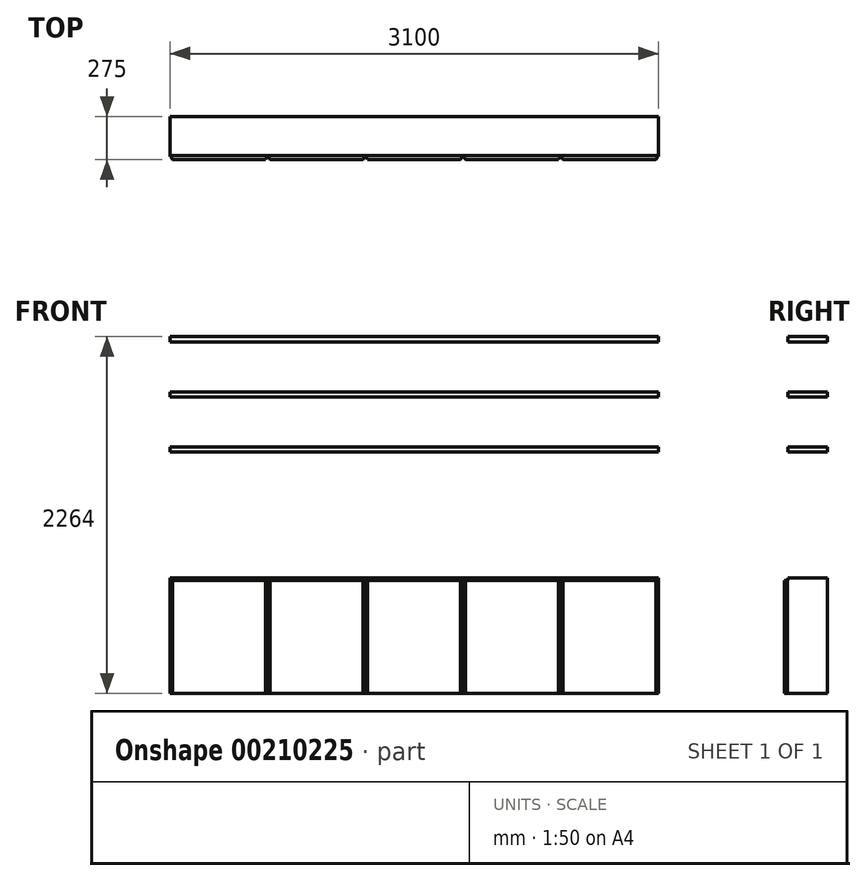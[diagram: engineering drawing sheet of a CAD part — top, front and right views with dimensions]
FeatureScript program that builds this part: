
annotation { "Feature Type Name" : "Feature", "Feature Type Description" : "" }
export const myFeature = defineFeature(function(context is Context, id is Id, definition is map)
    precondition{}
    {
        {
            var Q0;
            Q0=qCreatedBy(makeId("Right.planeOp"),FACE);
            var sketch = newSketch(context, id + "F0", { "sketchPlane" : qUnion([Q0])});
            skLineSegment(sketch, "E0.bottom", {"start": v(-250, 732) * mm, "end": v(0, 732) * mm});
            skLineSegment(sketch, "E0.top", {"start": v(-250, 700) * mm, "end": v(0, 700) * mm});
            skLineSegment(sketch, "E0.left", {"start": v(-250, 732) * mm, "end": v(-250, 700) * mm});
            skLineSegment(sketch, "E0.right", {"start": v(0, 732) * mm, "end": v(0, 700) * mm});
            skLineSegment(sketch, "E1.bottom", {"start": v(-250, 1532) * mm, "end": v(0, 1532) * mm});
            skLineSegment(sketch, "E1.top", {"start": v(-250, 1564) * mm, "end": v(0, 1564) * mm});
            skLineSegment(sketch, "E1.left", {"start": v(-250, 1532) * mm, "end": v(-250, 1564) * mm});
            skLineSegment(sketch, "E1.right", {"start": v(0, 1532) * mm, "end": v(0, 1564) * mm});
            skLineSegment(sketch, "E2.0.1.0", {"start": v(0, 1882) * mm, "end": v(0, 1914) * mm});
            skLineSegment(sketch, "E2.0.1.1", {"start": v(-250, 1882) * mm, "end": v(0, 1882) * mm});
            skLineSegment(sketch, "E2.0.1.2", {"start": v(-250, 1914) * mm, "end": v(0, 1914) * mm});
            skLineSegment(sketch, "E2.0.1.3", {"start": v(-250, 1882) * mm, "end": v(-250, 1914) * mm});
            skLineSegment(sketch, "E2.0.2.0", {"start": v(0, 2232) * mm, "end": v(0, 2264) * mm});
            skLineSegment(sketch, "E2.0.2.1", {"start": v(-250, 2232) * mm, "end": v(0, 2232) * mm});
            skLineSegment(sketch, "E2.0.2.2", {"start": v(-250, 2264) * mm, "end": v(0, 2264) * mm});
            skLineSegment(sketch, "E2.0.2.3", {"start": v(-250, 2232) * mm, "end": v(-250, 2264) * mm});
            skLineSegment(sketch, "E2.direction1", {"start": v(0, 1532) * mm, "end": v(310, 1532) * mm, "construction": true});
            skLineSegment(sketch, "E2.direction2", {"start": v(0, 1532) * mm, "end": v(0, 1882) * mm, "construction": true});
            skLineSegment(sketch, "E3", {"start": v(-529, 2600) * mm, "end": v(424, 2600) * mm, "construction": true});
            skSolve(sketch);
        }
        {
            var Q0;
            Q0=makeQuery(id+"F0.imprint","IMPRINT",FACE,{"disambiguationData":[TD([[makeQuery(id+"F0.imprint","IMPRINT",EDGE,{"derivedFrom":sQuery(id+"F0.wireOp",EDGE,"E0.bottom")}),-1.0]])]});
            var Q1;
            Q1=makeQuery(id+"F0.imprint","IMPRINT",FACE,{"disambiguationData":[TD([[makeQuery(id+"F0.imprint","IMPRINT",EDGE,{"derivedFrom":sQuery(id+"F0.wireOp",EDGE,"E1.bottom")}),1.0]])]});
            var Q2;
            Q2=makeQuery(id+"F0.imprint","IMPRINT",FACE,{"disambiguationData":[TD([[makeQuery(id+"F0.imprint","IMPRINT",EDGE,{"derivedFrom":sQuery(id+"F0.wireOp",EDGE,"E2.0.2.0")}),1.0]])]});
            var Q3;
            Q3=makeQuery(id+"F0.imprint","IMPRINT",FACE,{"disambiguationData":[TD([[makeQuery(id+"F0.imprint","IMPRINT",EDGE,{"derivedFrom":sQuery(id+"F0.wireOp",EDGE,"E2.0.1.0")}),1.0]])]});
            extrude(context, id + "F1", {"entities" : qUnion([Q0, Q1, Q2, Q3]), "depth" : 3100 * mm});
        }
        {
            var Q0;
            Q0=makeQuery(id+"F1.opExtrude","SWEPT_FACE",FACE,{"disambiguationData":[OSD([sQuery(id+"F0.wireOp",EDGE,"E0.left")])]});
            var sketch = newSketch(context, id + "F2", { "sketchPlane" : qUnion([Q0])});
            skLineSegment(sketch, "E4", {"start": v(0, 0) * mm, "end": v(3100, 0) * mm});
            skLineSegment(sketch, "E5", {"start": v(3100, 0) * mm, "end": v(3100, 716) * mm});
            skLineSegment(sketch, "E6", {"start": v(3100, 716) * mm, "end": v(0, 716) * mm});
            skLineSegment(sketch, "E7", {"start": v(0, 716) * mm, "end": v(0, 0) * mm});
            skLineSegment(sketch, "E8", {"start": v(0, 0) * mm, "end": v(0, 716) * mm});
            skLineSegment(sketch, "E9.1.0.0", {"start": v(620, 0) * mm, "end": v(620, 716) * mm});
            skLineSegment(sketch, "E9.2.0.0", {"start": v(1240, 0) * mm, "end": v(1240, 716) * mm});
            skLineSegment(sketch, "E9.3.0.0", {"start": v(1860, 0) * mm, "end": v(1860, 716) * mm});
            skLineSegment(sketch, "E9.direction1", {"start": v(0, 0) * mm, "end": v(620, 0) * mm, "construction": true});
            skLineSegment(sketch, "E10.0.4.0", {"start": v(2480, 0) * mm, "end": v(2480, 716) * mm});
            skLineSegment(sketch, "E11", {"start": v(32, 716) * mm, "end": v(32, 0) * mm});
            skLineSegment(sketch, "E12.bottom", {"start": v(636, 716) * mm, "end": v(604, 716) * mm});
            skLineSegment(sketch, "E12.top", {"start": v(636, 0) * mm, "end": v(604, 0) * mm});
            skLineSegment(sketch, "E12.left", {"start": v(636, 716) * mm, "end": v(636, 0) * mm});
            skLineSegment(sketch, "E12.right", {"start": v(604, 716) * mm, "end": v(604, 0) * mm});
            skPoint(sketch, "E12.middle", {"position": v(620, 358) * mm});
            skLineSegment(sketch, "E13", {"start": v(3068, 0) * mm, "end": v(3068, 716) * mm});
            skLineSegment(sketch, "E14.1.0.0", {"start": v(1256, 716) * mm, "end": v(1256, 0) * mm});
            skPoint(sketch, "E14.1.0.1", {"position": v(1240, 358) * mm});
            skLineSegment(sketch, "E14.1.0.2", {"start": v(1224, 716) * mm, "end": v(1224, 0) * mm});
            skLineSegment(sketch, "E14.1.0.3", {"start": v(1256, 716) * mm, "end": v(1224, 716) * mm});
            skLineSegment(sketch, "E14.1.0.4", {"start": v(1256, 0) * mm, "end": v(1224, 0) * mm});
            skLineSegment(sketch, "E14.2.0.0", {"start": v(1876, 716) * mm, "end": v(1876, 0) * mm});
            skPoint(sketch, "E14.2.0.1", {"position": v(1860, 358) * mm});
            skLineSegment(sketch, "E14.2.0.2", {"start": v(1844, 716) * mm, "end": v(1844, 0) * mm});
            skLineSegment(sketch, "E14.2.0.3", {"start": v(1876, 716) * mm, "end": v(1844, 716) * mm});
            skLineSegment(sketch, "E14.2.0.4", {"start": v(1876, 0) * mm, "end": v(1844, 0) * mm});
            skLineSegment(sketch, "E14.3.0.0", {"start": v(2496, 716) * mm, "end": v(2496, 0) * mm});
            skPoint(sketch, "E14.3.0.1", {"position": v(2480, 358) * mm});
            skLineSegment(sketch, "E14.3.0.2", {"start": v(2464, 716) * mm, "end": v(2464, 0) * mm});
            skLineSegment(sketch, "E14.3.0.3", {"start": v(2496, 716) * mm, "end": v(2464, 716) * mm});
            skLineSegment(sketch, "E14.3.0.4", {"start": v(2496, 0) * mm, "end": v(2464, 0) * mm});
            skLineSegment(sketch, "E14.direction1", {"start": v(604, 0) * mm, "end": v(1224, 0) * mm, "construction": true});
            skSolve(sketch);
        }
        {
            var Q0;
            {var subQ0=sQuery(id+"F2.wireOp",EDGE,"E8");var subQ1=sQuery(id+"F2.wireOp",EDGE,"E4");var subQ2=makeQuery(id+"F2.imprint","INTERSECT",VERTEX,{"derivedFrom":[subQ1,subQ0]});Q0=makeQuery(id+"F2.imprint","IMPRINT",FACE,{"disambiguationData":[TD([[makeQuery(id+"F2.imprint","IMPRINT",EDGE,{"disambiguationData":[TD([[subQ2,-1.0]])],"derivedFrom":subQ1}),1.0]])]});}
            var Q1;
            {var subQ0=sQuery(id+"F2.wireOp",EDGE,"E12.top");var subQ1=sQuery(id+"F2.wireOp",EDGE,"E9.1.0.0");var subQ2=makeQuery(id+"F2.imprint","INTERSECT",VERTEX,{"derivedFrom":[subQ1,subQ0]});Q1=makeQuery(id+"F2.imprint","IMPRINT",FACE,{"disambiguationData":[TD([[makeQuery(id+"F2.imprint","IMPRINT",EDGE,{"disambiguationData":[TD([[subQ2,-1.0]])],"derivedFrom":subQ1}),1.0]])]});}
            var Q2;
            {var subQ0=sQuery(id+"F2.wireOp",EDGE,"E12.top");var subQ1=sQuery(id+"F2.wireOp",EDGE,"E9.1.0.0");var subQ2=makeQuery(id+"F2.imprint","INTERSECT",VERTEX,{"derivedFrom":[subQ1,subQ0]});Q2=makeQuery(id+"F2.imprint","IMPRINT",FACE,{"disambiguationData":[TD([[makeQuery(id+"F2.imprint","IMPRINT",EDGE,{"disambiguationData":[TD([[subQ2,-1.0]])],"derivedFrom":subQ1}),-1.0]])]});}
            var Q3;
            {var subQ0=sQuery(id+"F2.wireOp",EDGE,"E14.1.0.4");var subQ1=sQuery(id+"F2.wireOp",EDGE,"E9.2.0.0");var subQ2=makeQuery(id+"F2.imprint","INTERSECT",VERTEX,{"derivedFrom":[subQ1,subQ0]});Q3=makeQuery(id+"F2.imprint","IMPRINT",FACE,{"disambiguationData":[TD([[makeQuery(id+"F2.imprint","IMPRINT",EDGE,{"disambiguationData":[TD([[subQ2,-1.0]])],"derivedFrom":subQ1}),1.0]])]});}
            var Q4;
            {var subQ0=sQuery(id+"F2.wireOp",EDGE,"E14.1.0.4");var subQ1=sQuery(id+"F2.wireOp",EDGE,"E9.2.0.0");var subQ2=makeQuery(id+"F2.imprint","INTERSECT",VERTEX,{"derivedFrom":[subQ1,subQ0]});Q4=makeQuery(id+"F2.imprint","IMPRINT",FACE,{"disambiguationData":[TD([[makeQuery(id+"F2.imprint","IMPRINT",EDGE,{"disambiguationData":[TD([[subQ2,-1.0]])],"derivedFrom":subQ1}),-1.0]])]});}
            var Q5;
            {var subQ0=sQuery(id+"F2.wireOp",EDGE,"E14.2.0.4");var subQ1=sQuery(id+"F2.wireOp",EDGE,"E9.3.0.0");var subQ2=makeQuery(id+"F2.imprint","INTERSECT",VERTEX,{"derivedFrom":[subQ1,subQ0]});Q5=makeQuery(id+"F2.imprint","IMPRINT",FACE,{"disambiguationData":[TD([[makeQuery(id+"F2.imprint","IMPRINT",EDGE,{"disambiguationData":[TD([[subQ2,-1.0]])],"derivedFrom":subQ1}),-1.0]])]});}
            var Q6;
            {var subQ0=sQuery(id+"F2.wireOp",EDGE,"E14.2.0.4");var subQ1=sQuery(id+"F2.wireOp",EDGE,"E9.3.0.0");var subQ2=makeQuery(id+"F2.imprint","INTERSECT",VERTEX,{"derivedFrom":[subQ1,subQ0]});Q6=makeQuery(id+"F2.imprint","IMPRINT",FACE,{"disambiguationData":[TD([[makeQuery(id+"F2.imprint","IMPRINT",EDGE,{"disambiguationData":[TD([[subQ2,-1.0]])],"derivedFrom":subQ1}),1.0]])]});}
            var Q7;
            {var subQ0=sQuery(id+"F2.wireOp",EDGE,"E14.3.0.4");var subQ1=sQuery(id+"F2.wireOp",EDGE,"E10.0.4.0");var subQ2=makeQuery(id+"F2.imprint","INTERSECT",VERTEX,{"derivedFrom":[subQ1,subQ0]});Q7=makeQuery(id+"F2.imprint","IMPRINT",FACE,{"disambiguationData":[TD([[makeQuery(id+"F2.imprint","IMPRINT",EDGE,{"disambiguationData":[TD([[subQ2,-1.0]])],"derivedFrom":subQ1}),-1.0]])]});}
            var Q8;
            {var subQ0=sQuery(id+"F2.wireOp",EDGE,"E14.3.0.4");var subQ1=sQuery(id+"F2.wireOp",EDGE,"E10.0.4.0");var subQ2=makeQuery(id+"F2.imprint","INTERSECT",VERTEX,{"derivedFrom":[subQ1,subQ0]});Q8=makeQuery(id+"F2.imprint","IMPRINT",FACE,{"disambiguationData":[TD([[makeQuery(id+"F2.imprint","IMPRINT",EDGE,{"disambiguationData":[TD([[subQ2,-1.0]])],"derivedFrom":subQ1}),1.0]])]});}
            var Q9;
            {var subQ0=sQuery(id+"F2.wireOp",EDGE,"E5");var subQ1=sQuery(id+"F2.wireOp",EDGE,"E4");var subQ2=makeQuery(id+"F2.imprint","INTERSECT",VERTEX,{"derivedFrom":[subQ1,subQ0]});Q9=makeQuery(id+"F2.imprint","IMPRINT",FACE,{"disambiguationData":[TD([[makeQuery(id+"F2.imprint","IMPRINT",EDGE,{"disambiguationData":[TD([[subQ2,1.0]])],"derivedFrom":subQ1}),1.0]])]});}
            var Q10;
            Q10=makeQuery(id+"F1.opExtrude","SWEPT_FACE",FACE,{"disambiguationData":[OSD([sQuery(id+"F0.wireOp",EDGE,"E0.right")])]});
            extrude(context, id + "F3", {"entities" : qUnion([Q0, Q1, Q2, Q3, Q4, Q5, Q6, Q7, Q8, Q9]), "operationType" : NewBodyOperationType.ADD, "endBound" : BoundingType.UP_TO_SURFACE, "oppositeDirection" : true, "endBoundEntityFace" : qUnion([Q10]), "depth" : 25 * mm});
        }
        {
            var Q0;
            {var subQ0=sQuery(id+"F2.wireOp",EDGE,"E8");var subQ1=sQuery(id+"F2.wireOp",EDGE,"E4");var subQ2=makeQuery(id+"F2.imprint","INTERSECT",VERTEX,{"derivedFrom":[subQ1,subQ0]});Q0=makeQuery(id+"F2.imprint","IMPRINT",FACE,{"disambiguationData":[TD([[makeQuery(id+"F2.imprint","IMPRINT",EDGE,{"disambiguationData":[TD([[subQ2,-1.0]])],"derivedFrom":subQ1}),1.0]])]});}
            var Q1;
            {var subQ1=sQuery(id+"F2.wireOp",EDGE,"E6");var subQ4=sQuery(id+"F2.wireOp",EDGE,"E11");var subQ5=makeQuery(id+"F2.imprint","INTERSECT",VERTEX,{"derivedFrom":[subQ1,subQ4]});Q1=makeQuery(id+"F2.imprint","IMPRINT",FACE,{"disambiguationData":[TD([[makeQuery(id+"F2.imprint","IMPRINT",EDGE,{"disambiguationData":[TD([[subQ5,-1.0]])],"derivedFrom":subQ1}),1.0]])]});}
            var Q2;
            {var subQ0=sQuery(id+"F2.wireOp",EDGE,"E11");var subQ1=sQuery(id+"F2.wireOp",EDGE,"E6");var subQ2=makeQuery(id+"F2.imprint","INTERSECT",VERTEX,{"derivedFrom":[subQ1,subQ0]});Q2=makeQuery(id+"F2.imprint","IMPRINT",FACE,{"disambiguationData":[TD([[makeQuery(id+"F2.imprint","IMPRINT",EDGE,{"disambiguationData":[TD([[subQ2,1.0]])],"derivedFrom":subQ1}),1.0]])]});}
            var Q3;
            {var subQ0=sQuery(id+"F2.wireOp",EDGE,"E11");var subQ1=sQuery(id+"F2.wireOp",EDGE,"E4");var subQ2=makeQuery(id+"F2.imprint","INTERSECT",VERTEX,{"derivedFrom":[subQ1,subQ0]});Q3=makeQuery(id+"F2.imprint","IMPRINT",FACE,{"disambiguationData":[TD([[makeQuery(id+"F2.imprint","IMPRINT",EDGE,{"disambiguationData":[TD([[subQ2,-1.0]])],"derivedFrom":subQ1}),1.0]])]});}
            var Q4;
            {var subQ0=sQuery(id+"F2.wireOp",EDGE,"E12.top");var subQ1=sQuery(id+"F2.wireOp",EDGE,"E9.1.0.0");var subQ2=makeQuery(id+"F2.imprint","INTERSECT",VERTEX,{"derivedFrom":[subQ1,subQ0]});Q4=makeQuery(id+"F2.imprint","IMPRINT",FACE,{"disambiguationData":[TD([[makeQuery(id+"F2.imprint","IMPRINT",EDGE,{"disambiguationData":[TD([[subQ2,-1.0]])],"derivedFrom":subQ1}),1.0]])]});}
            var Q5;
            {var subQ0=sQuery(id+"F2.wireOp",EDGE,"E12.bottom");var subQ1=sQuery(id+"F2.wireOp",EDGE,"E9.1.0.0");var subQ2=makeQuery(id+"F2.imprint","INTERSECT",VERTEX,{"derivedFrom":[subQ1,subQ0]});Q5=makeQuery(id+"F2.imprint","IMPRINT",FACE,{"disambiguationData":[TD([[makeQuery(id+"F2.imprint","IMPRINT",EDGE,{"disambiguationData":[TD([[subQ2,1.0]])],"derivedFrom":subQ1}),1.0]])]});}
            var Q6;
            {var subQ0=sQuery(id+"F2.wireOp",EDGE,"E12.left");var subQ1=sQuery(id+"F2.wireOp",EDGE,"E4");var subQ2=makeQuery(id+"F2.imprint","INTERSECT",VERTEX,{"derivedFrom":[subQ1,sQuery(id+"F2.wireOp",EDGE,"E12.top"),subQ0]});Q6=makeQuery(id+"F2.imprint","IMPRINT",FACE,{"disambiguationData":[TD([[makeQuery(id+"F2.imprint","IMPRINT",EDGE,{"disambiguationData":[TD([[subQ2,-1.0]])],"derivedFrom":subQ1}),1.0]])]});}
            var Q7;
            {var subQ0=sQuery(id+"F2.wireOp",EDGE,"E12.top");var subQ1=sQuery(id+"F2.wireOp",EDGE,"E9.1.0.0");var subQ2=makeQuery(id+"F2.imprint","INTERSECT",VERTEX,{"derivedFrom":[subQ1,subQ0]});Q7=makeQuery(id+"F2.imprint","IMPRINT",FACE,{"disambiguationData":[TD([[makeQuery(id+"F2.imprint","IMPRINT",EDGE,{"disambiguationData":[TD([[subQ2,-1.0]])],"derivedFrom":subQ1}),-1.0]])]});}
            var Q8;
            {var subQ0=sQuery(id+"F2.wireOp",EDGE,"E12.bottom");var subQ1=sQuery(id+"F2.wireOp",EDGE,"E9.1.0.0");var subQ2=makeQuery(id+"F2.imprint","INTERSECT",VERTEX,{"derivedFrom":[subQ1,subQ0]});Q8=makeQuery(id+"F2.imprint","IMPRINT",FACE,{"disambiguationData":[TD([[makeQuery(id+"F2.imprint","IMPRINT",EDGE,{"disambiguationData":[TD([[subQ2,1.0]])],"derivedFrom":subQ1}),-1.0]])]});}
            var Q9;
            {var subQ0=sQuery(id+"F2.wireOp",EDGE,"E12.left");var subQ1=sQuery(id+"F2.wireOp",EDGE,"E6");var subQ2=makeQuery(id+"F2.imprint","INTERSECT",VERTEX,{"derivedFrom":[subQ1,sQuery(id+"F2.wireOp",EDGE,"E12.bottom"),subQ0]});Q9=makeQuery(id+"F2.imprint","IMPRINT",FACE,{"disambiguationData":[TD([[makeQuery(id+"F2.imprint","IMPRINT",EDGE,{"disambiguationData":[TD([[subQ2,1.0]])],"derivedFrom":subQ1}),1.0]])]});}
            var Q10;
            {var subQ0=sQuery(id+"F2.wireOp",EDGE,"E14.1.0.3");var subQ1=sQuery(id+"F2.wireOp",EDGE,"E9.2.0.0");var subQ2=makeQuery(id+"F2.imprint","INTERSECT",VERTEX,{"derivedFrom":[subQ1,subQ0]});Q10=makeQuery(id+"F2.imprint","IMPRINT",FACE,{"disambiguationData":[TD([[makeQuery(id+"F2.imprint","IMPRINT",EDGE,{"disambiguationData":[TD([[subQ2,1.0]])],"derivedFrom":subQ1}),1.0]])]});}
            var Q11;
            {var subQ0=sQuery(id+"F2.wireOp",EDGE,"E14.1.0.4");var subQ1=sQuery(id+"F2.wireOp",EDGE,"E9.2.0.0");var subQ2=makeQuery(id+"F2.imprint","INTERSECT",VERTEX,{"derivedFrom":[subQ1,subQ0]});Q11=makeQuery(id+"F2.imprint","IMPRINT",FACE,{"disambiguationData":[TD([[makeQuery(id+"F2.imprint","IMPRINT",EDGE,{"disambiguationData":[TD([[subQ2,-1.0]])],"derivedFrom":subQ1}),1.0]])]});}
            var Q12;
            {var subQ0=sQuery(id+"F2.wireOp",EDGE,"E14.1.0.4");var subQ1=sQuery(id+"F2.wireOp",EDGE,"E9.2.0.0");var subQ2=makeQuery(id+"F2.imprint","INTERSECT",VERTEX,{"derivedFrom":[subQ1,subQ0]});Q12=makeQuery(id+"F2.imprint","IMPRINT",FACE,{"disambiguationData":[TD([[makeQuery(id+"F2.imprint","IMPRINT",EDGE,{"disambiguationData":[TD([[subQ2,-1.0]])],"derivedFrom":subQ1}),-1.0]])]});}
            var Q13;
            {var subQ0=sQuery(id+"F2.wireOp",EDGE,"E14.1.0.3");var subQ1=sQuery(id+"F2.wireOp",EDGE,"E9.2.0.0");var subQ2=makeQuery(id+"F2.imprint","INTERSECT",VERTEX,{"derivedFrom":[subQ1,subQ0]});Q13=makeQuery(id+"F2.imprint","IMPRINT",FACE,{"disambiguationData":[TD([[makeQuery(id+"F2.imprint","IMPRINT",EDGE,{"disambiguationData":[TD([[subQ2,1.0]])],"derivedFrom":subQ1}),-1.0]])]});}
            var Q14;
            {var subQ0=sQuery(id+"F2.wireOp",EDGE,"E14.1.0.0");var subQ1=sQuery(id+"F2.wireOp",EDGE,"E6");var subQ2=makeQuery(id+"F2.imprint","INTERSECT",VERTEX,{"derivedFrom":[subQ1,subQ0,sQuery(id+"F2.wireOp",EDGE,"E14.1.0.3")]});Q14=makeQuery(id+"F2.imprint","IMPRINT",FACE,{"disambiguationData":[TD([[makeQuery(id+"F2.imprint","IMPRINT",EDGE,{"disambiguationData":[TD([[subQ2,1.0]])],"derivedFrom":subQ1}),1.0]])]});}
            var Q15;
            {var subQ0=sQuery(id+"F2.wireOp",EDGE,"E14.1.0.0");var subQ1=sQuery(id+"F2.wireOp",EDGE,"E4");var subQ2=makeQuery(id+"F2.imprint","INTERSECT",VERTEX,{"derivedFrom":[subQ1,subQ0,sQuery(id+"F2.wireOp",EDGE,"E14.1.0.4")]});Q15=makeQuery(id+"F2.imprint","IMPRINT",FACE,{"disambiguationData":[TD([[makeQuery(id+"F2.imprint","IMPRINT",EDGE,{"disambiguationData":[TD([[subQ2,-1.0]])],"derivedFrom":subQ1}),1.0]])]});}
            var Q16;
            {var subQ0=sQuery(id+"F2.wireOp",EDGE,"E14.2.0.3");var subQ1=sQuery(id+"F2.wireOp",EDGE,"E9.3.0.0");var subQ2=makeQuery(id+"F2.imprint","INTERSECT",VERTEX,{"derivedFrom":[subQ1,subQ0]});Q16=makeQuery(id+"F2.imprint","IMPRINT",FACE,{"disambiguationData":[TD([[makeQuery(id+"F2.imprint","IMPRINT",EDGE,{"disambiguationData":[TD([[subQ2,1.0]])],"derivedFrom":subQ1}),1.0]])]});}
            var Q17;
            {var subQ0=sQuery(id+"F2.wireOp",EDGE,"E14.2.0.4");var subQ1=sQuery(id+"F2.wireOp",EDGE,"E9.3.0.0");var subQ2=makeQuery(id+"F2.imprint","INTERSECT",VERTEX,{"derivedFrom":[subQ1,subQ0]});Q17=makeQuery(id+"F2.imprint","IMPRINT",FACE,{"disambiguationData":[TD([[makeQuery(id+"F2.imprint","IMPRINT",EDGE,{"disambiguationData":[TD([[subQ2,-1.0]])],"derivedFrom":subQ1}),1.0]])]});}
            var Q18;
            {var subQ0=sQuery(id+"F2.wireOp",EDGE,"E14.2.0.4");var subQ1=sQuery(id+"F2.wireOp",EDGE,"E9.3.0.0");var subQ2=makeQuery(id+"F2.imprint","INTERSECT",VERTEX,{"derivedFrom":[subQ1,subQ0]});Q18=makeQuery(id+"F2.imprint","IMPRINT",FACE,{"disambiguationData":[TD([[makeQuery(id+"F2.imprint","IMPRINT",EDGE,{"disambiguationData":[TD([[subQ2,-1.0]])],"derivedFrom":subQ1}),-1.0]])]});}
            var Q19;
            {var subQ0=sQuery(id+"F2.wireOp",EDGE,"E14.2.0.3");var subQ1=sQuery(id+"F2.wireOp",EDGE,"E9.3.0.0");var subQ2=makeQuery(id+"F2.imprint","INTERSECT",VERTEX,{"derivedFrom":[subQ1,subQ0]});Q19=makeQuery(id+"F2.imprint","IMPRINT",FACE,{"disambiguationData":[TD([[makeQuery(id+"F2.imprint","IMPRINT",EDGE,{"disambiguationData":[TD([[subQ2,1.0]])],"derivedFrom":subQ1}),-1.0]])]});}
            var Q20;
            {var subQ0=sQuery(id+"F2.wireOp",EDGE,"E14.2.0.0");var subQ1=sQuery(id+"F2.wireOp",EDGE,"E6");var subQ2=makeQuery(id+"F2.imprint","INTERSECT",VERTEX,{"derivedFrom":[subQ1,subQ0,sQuery(id+"F2.wireOp",EDGE,"E14.2.0.3")]});Q20=makeQuery(id+"F2.imprint","IMPRINT",FACE,{"disambiguationData":[TD([[makeQuery(id+"F2.imprint","IMPRINT",EDGE,{"disambiguationData":[TD([[subQ2,1.0]])],"derivedFrom":subQ1}),1.0]])]});}
            var Q21;
            {var subQ0=sQuery(id+"F2.wireOp",EDGE,"E14.2.0.0");var subQ1=sQuery(id+"F2.wireOp",EDGE,"E4");var subQ2=makeQuery(id+"F2.imprint","INTERSECT",VERTEX,{"derivedFrom":[subQ1,subQ0,sQuery(id+"F2.wireOp",EDGE,"E14.2.0.4")]});Q21=makeQuery(id+"F2.imprint","IMPRINT",FACE,{"disambiguationData":[TD([[makeQuery(id+"F2.imprint","IMPRINT",EDGE,{"disambiguationData":[TD([[subQ2,-1.0]])],"derivedFrom":subQ1}),1.0]])]});}
            var Q22;
            {var subQ0=sQuery(id+"F2.wireOp",EDGE,"E14.3.0.3");var subQ1=sQuery(id+"F2.wireOp",EDGE,"E10.0.4.0");var subQ2=makeQuery(id+"F2.imprint","INTERSECT",VERTEX,{"derivedFrom":[subQ1,subQ0]});Q22=makeQuery(id+"F2.imprint","IMPRINT",FACE,{"disambiguationData":[TD([[makeQuery(id+"F2.imprint","IMPRINT",EDGE,{"disambiguationData":[TD([[subQ2,1.0]])],"derivedFrom":subQ1}),1.0]])]});}
            var Q23;
            {var subQ0=sQuery(id+"F2.wireOp",EDGE,"E14.3.0.4");var subQ1=sQuery(id+"F2.wireOp",EDGE,"E10.0.4.0");var subQ2=makeQuery(id+"F2.imprint","INTERSECT",VERTEX,{"derivedFrom":[subQ1,subQ0]});Q23=makeQuery(id+"F2.imprint","IMPRINT",FACE,{"disambiguationData":[TD([[makeQuery(id+"F2.imprint","IMPRINT",EDGE,{"disambiguationData":[TD([[subQ2,-1.0]])],"derivedFrom":subQ1}),1.0]])]});}
            var Q24;
            {var subQ0=sQuery(id+"F2.wireOp",EDGE,"E14.3.0.4");var subQ1=sQuery(id+"F2.wireOp",EDGE,"E10.0.4.0");var subQ2=makeQuery(id+"F2.imprint","INTERSECT",VERTEX,{"derivedFrom":[subQ1,subQ0]});Q24=makeQuery(id+"F2.imprint","IMPRINT",FACE,{"disambiguationData":[TD([[makeQuery(id+"F2.imprint","IMPRINT",EDGE,{"disambiguationData":[TD([[subQ2,-1.0]])],"derivedFrom":subQ1}),-1.0]])]});}
            var Q25;
            {var subQ0=sQuery(id+"F2.wireOp",EDGE,"E14.3.0.3");var subQ1=sQuery(id+"F2.wireOp",EDGE,"E10.0.4.0");var subQ2=makeQuery(id+"F2.imprint","INTERSECT",VERTEX,{"derivedFrom":[subQ1,subQ0]});Q25=makeQuery(id+"F2.imprint","IMPRINT",FACE,{"disambiguationData":[TD([[makeQuery(id+"F2.imprint","IMPRINT",EDGE,{"disambiguationData":[TD([[subQ2,1.0]])],"derivedFrom":subQ1}),-1.0]])]});}
            var Q26;
            {var subQ0=sQuery(id+"F2.wireOp",EDGE,"E13");var subQ1=sQuery(id+"F2.wireOp",EDGE,"E6");var subQ2=makeQuery(id+"F2.imprint","INTERSECT",VERTEX,{"derivedFrom":[subQ1,subQ0]});Q26=makeQuery(id+"F2.imprint","IMPRINT",FACE,{"disambiguationData":[TD([[makeQuery(id+"F2.imprint","IMPRINT",EDGE,{"disambiguationData":[TD([[subQ2,-1.0]])],"derivedFrom":subQ1}),1.0]])]});}
            var Q27;
            {var subQ0=sQuery(id+"F2.wireOp",EDGE,"E13");var subQ1=sQuery(id+"F2.wireOp",EDGE,"E4");var subQ2=makeQuery(id+"F2.imprint","INTERSECT",VERTEX,{"derivedFrom":[subQ1,subQ0]});Q27=makeQuery(id+"F2.imprint","IMPRINT",FACE,{"disambiguationData":[TD([[makeQuery(id+"F2.imprint","IMPRINT",EDGE,{"disambiguationData":[TD([[subQ2,1.0]])],"derivedFrom":subQ1}),1.0]])]});}
            var Q28;
            {var subQ0=sQuery(id+"F2.wireOp",EDGE,"E5");var subQ1=sQuery(id+"F2.wireOp",EDGE,"E4");var subQ2=makeQuery(id+"F2.imprint","INTERSECT",VERTEX,{"derivedFrom":[subQ1,subQ0]});Q28=makeQuery(id+"F2.imprint","IMPRINT",FACE,{"disambiguationData":[TD([[makeQuery(id+"F2.imprint","IMPRINT",EDGE,{"disambiguationData":[TD([[subQ2,1.0]])],"derivedFrom":subQ1}),1.0]])]});}
            var Q29;
            {var subQ1=sQuery(id+"F2.wireOp",EDGE,"E6");var subQ4=sQuery(id+"F2.wireOp",EDGE,"E13");var subQ5=makeQuery(id+"F2.imprint","INTERSECT",VERTEX,{"derivedFrom":[subQ1,subQ4]});Q29=makeQuery(id+"F2.imprint","IMPRINT",FACE,{"disambiguationData":[TD([[makeQuery(id+"F2.imprint","IMPRINT",EDGE,{"disambiguationData":[TD([[subQ5,1.0]])],"derivedFrom":subQ1}),1.0]])]});}
            extrude(context, id + "F4", {"entities" : qUnion([Q0, Q1, Q2, Q3, Q4, Q5, Q6, Q7, Q8, Q9, Q10, Q11, Q12, Q13, Q14, Q15, Q16, Q17, Q18, Q19, Q20, Q21, Q22, Q23, Q24, Q25, Q26, Q27, Q28, Q29]), "operationType" : NewBodyOperationType.ADD, "depth" : 25 * mm});
        }
        {
            var Q0;
            Q0=makeQuery(id+"F4.opExtrude","SWEPT_FACE",FACE,{"disambiguationData":[OSD([sQuery(id+"F2.wireOp",EDGE,"E6")])]});
            var sketch = newSketch(context, id + "F5", { "sketchPlane" : qUnion([Q0])});
            skLineSegment(sketch, "E15", {"start": v(0, -250) * mm, "end": v(-2.89, -255) * mm});
            skLineSegment(sketch, "E16", {"start": v(-14.43, -275) * mm, "end": v(14.43, -275) * mm});
            skLineSegment(sketch, "E17", {"start": v(14.43, -275) * mm, "end": v(2.89, -255) * mm});
            skLineSegment(sketch, "E18", {"start": v(-2.89, -255) * mm, "end": v(2.89, -255) * mm});
            skLineSegment(sketch, "E19", {"start": v(-2.89, -255) * mm, "end": v(-14.43, -275) * mm});
            skLineSegment(sketch, "E20", {"start": v(2.89, -255) * mm, "end": v(0, -250) * mm});
            skLineSegment(sketch, "E21.1.0.0", {"start": v(617.11, -255) * mm, "end": v(605.57, -275) * mm});
            skLineSegment(sketch, "E21.1.0.1", {"start": v(617.11, -255) * mm, "end": v(622.89, -255) * mm});
            skLineSegment(sketch, "E21.1.0.2", {"start": v(634.43, -275) * mm, "end": v(622.89, -255) * mm});
            skLineSegment(sketch, "E21.1.0.3", {"start": v(605.57, -275) * mm, "end": v(634.43, -275) * mm});
            skLineSegment(sketch, "E21.1.0.4", {"start": v(622.89, -255) * mm, "end": v(620, -250) * mm});
            skLineSegment(sketch, "E21.1.0.5", {"start": v(620, -250) * mm, "end": v(617.11, -255) * mm});
            skLineSegment(sketch, "E21.2.0.0", {"start": v(1237.11, -255) * mm, "end": v(1225.57, -275) * mm});
            skLineSegment(sketch, "E21.2.0.1", {"start": v(1237.11, -255) * mm, "end": v(1242.89, -255) * mm});
            skLineSegment(sketch, "E21.2.0.2", {"start": v(1254.43, -275) * mm, "end": v(1242.89, -255) * mm});
            skLineSegment(sketch, "E21.2.0.3", {"start": v(1225.57, -275) * mm, "end": v(1254.43, -275) * mm});
            skLineSegment(sketch, "E21.2.0.4", {"start": v(1242.89, -255) * mm, "end": v(1240, -250) * mm});
            skLineSegment(sketch, "E21.2.0.5", {"start": v(1240, -250) * mm, "end": v(1237.11, -255) * mm});
            skLineSegment(sketch, "E21.3.0.0", {"start": v(1857.11, -255) * mm, "end": v(1845.57, -275) * mm});
            skLineSegment(sketch, "E21.3.0.1", {"start": v(1857.11, -255) * mm, "end": v(1862.89, -255) * mm});
            skLineSegment(sketch, "E21.3.0.2", {"start": v(1874.43, -275) * mm, "end": v(1862.89, -255) * mm});
            skLineSegment(sketch, "E21.3.0.3", {"start": v(1845.57, -275) * mm, "end": v(1874.43, -275) * mm});
            skLineSegment(sketch, "E21.3.0.4", {"start": v(1862.89, -255) * mm, "end": v(1860, -250) * mm});
            skLineSegment(sketch, "E21.3.0.5", {"start": v(1860, -250) * mm, "end": v(1857.11, -255) * mm});
            skLineSegment(sketch, "E21.4.0.0", {"start": v(2477.11, -255) * mm, "end": v(2465.57, -275) * mm});
            skLineSegment(sketch, "E21.4.0.1", {"start": v(2477.11, -255) * mm, "end": v(2482.89, -255) * mm});
            skLineSegment(sketch, "E21.4.0.2", {"start": v(2494.43, -275) * mm, "end": v(2482.89, -255) * mm});
            skLineSegment(sketch, "E21.4.0.3", {"start": v(2465.57, -275) * mm, "end": v(2494.43, -275) * mm});
            skLineSegment(sketch, "E21.4.0.4", {"start": v(2482.89, -255) * mm, "end": v(2480, -250) * mm});
            skLineSegment(sketch, "E21.4.0.5", {"start": v(2480, -250) * mm, "end": v(2477.11, -255) * mm});
            skLineSegment(sketch, "E21.5.0.0", {"start": v(3097.11, -255) * mm, "end": v(3085.57, -275) * mm});
            skLineSegment(sketch, "E21.5.0.1", {"start": v(3097.11, -255) * mm, "end": v(3102.89, -255) * mm});
            skLineSegment(sketch, "E21.5.0.2", {"start": v(3114.43, -275) * mm, "end": v(3102.89, -255) * mm});
            skLineSegment(sketch, "E21.5.0.3", {"start": v(3085.57, -275) * mm, "end": v(3114.43, -275) * mm});
            skLineSegment(sketch, "E21.5.0.4", {"start": v(3102.89, -255) * mm, "end": v(3100, -250) * mm});
            skLineSegment(sketch, "E21.5.0.5", {"start": v(3100, -250) * mm, "end": v(3097.11, -255) * mm});
            skLineSegment(sketch, "E21.direction1", {"start": v(-14.43, -275) * mm, "end": v(605.57, -275) * mm, "construction": true});
            skSolve(sketch);
        }
        {
            var Q0;
            {var subQ4=sQuery(id+"F5.wireOp",EDGE,"E17");Q0=makeQuery(id+"F5.imprint","IMPRINT",FACE,{"disambiguationData":[TD([[makeQuery(id+"F5.imprint","IMPRINT",EDGE,{"derivedFrom":subQ4}),1.0]])]});}
            var Q1;
            Q1=makeQuery(id+"F5.imprint","IMPRINT",FACE,{"disambiguationData":[TD([[makeQuery(id+"F5.imprint","IMPRINT",EDGE,{"derivedFrom":sQuery(id+"F5.wireOp",EDGE,"E21.1.0.0")}),1.0]])]});
            var Q2;
            Q2=makeQuery(id+"F5.imprint","IMPRINT",FACE,{"disambiguationData":[TD([[makeQuery(id+"F5.imprint","IMPRINT",EDGE,{"derivedFrom":sQuery(id+"F5.wireOp",EDGE,"E21.2.0.0")}),1.0]])]});
            var Q3;
            Q3=makeQuery(id+"F5.imprint","IMPRINT",FACE,{"disambiguationData":[TD([[makeQuery(id+"F5.imprint","IMPRINT",EDGE,{"derivedFrom":sQuery(id+"F5.wireOp",EDGE,"E21.3.0.0")}),1.0]])]});
            var Q4;
            Q4=makeQuery(id+"F5.imprint","IMPRINT",FACE,{"disambiguationData":[TD([[makeQuery(id+"F5.imprint","IMPRINT",EDGE,{"derivedFrom":sQuery(id+"F5.wireOp",EDGE,"E21.4.0.0")}),1.0]])]});
            var Q5;
            {var subQ0=sQuery(id+"F5.wireOp",EDGE,"E21.5.0.0");Q5=makeQuery(id+"F5.imprint","IMPRINT",FACE,{"disambiguationData":[TD([[makeQuery(id+"F5.imprint","IMPRINT",EDGE,{"derivedFrom":subQ0}),1.0]])]});}
            extrude(context, id + "F6", {"entities" : qUnion([Q0, Q1, Q2, Q3, Q4, Q5]), "operationType" : NewBodyOperationType.REMOVE, "endBound" : BoundingType.UP_TO_NEXT, "oppositeDirection" : true, "depth" : 25 * mm});
        }
        {
            var Q0;
            Q0=makeQuery(id+"F1.opExtrude","SWEPT_FACE",FACE,{"disambiguationData":[OSD([sQuery(id+"F0.wireOp",EDGE,"E0.right")])]});
            var sketch = newSketch(context, id + "F7", { "sketchPlane" : qUnion([Q0])});
            skLineSegment(sketch, "E22", {"start": v(0, 0) * mm, "end": v(-3100, 0) * mm});
            skSolve(sketch);
        }
    });
